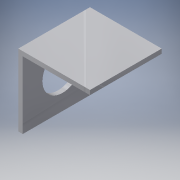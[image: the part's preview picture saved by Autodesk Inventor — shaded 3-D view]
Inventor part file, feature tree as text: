
AUTODESK INVENTOR PART (.ipt)
format: ipt  version: 2016 (Build 200138000, 138)  size: 105,984 bytes
history: native  units: in
note: dims shown in document units (in); Inventor stores cm internally (conversion verified against a paired STEP export)
features: extrude x2, sketch x2
ambient origin geometry x8: Origin, YZ Plane, XZ Plane, XY Plane, X Axis, Y Axis, Z Axis, Center Point
bodies: Solid1 (feature_tree)
feature tree (4):
  extrude  "Extrusion1"  Depth=2.0in
  extrude  "Extrusion2"  Depth=0.125in
  sketch  "Sketch1"  dims[d0=2.0in d1=2.0in]
  sketch  "Sketch2"  dims[d2=0.125in d3=0.125in d4=2.0in d5=0.0in d6=1.0in d7=1.0in d8=1.125in d9=2.0in d10=0.0in]
